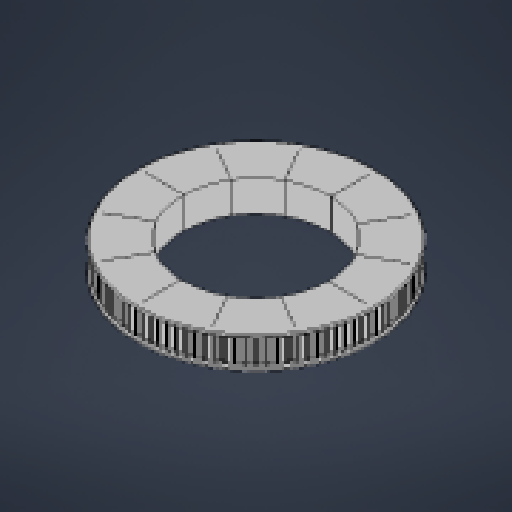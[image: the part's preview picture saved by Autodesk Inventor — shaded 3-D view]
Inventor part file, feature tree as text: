
AUTODESK INVENTOR PART (.ipt)
format: ipt  version: 2024 (Build 280153000, 153)  size: 1,488,896 bytes
history: native  units: mm
features: extrude x8, sketch x6, other x4, fillet x3, pattern_circular x2, revolve x1, mirror x1, hole x1, reference x1, projected_geometry x1
ambient origin geometry x8: Origin, YZ Plane, XZ Plane, XY Plane, X Axis, Y Axis, Z Axis, Center Point
bodies: Solid1 (feature_tree)
feature tree (28):
  extrude  "Extrusion1"  Depth=21.0mm
  extrude  "Extrusion2"  Depth=5.8mm
  extrude  "Extrusion3"  Depth=21.0mm
  fillet  "Fillet2"  [1 undecoded]
  pattern_circular  "Circular Pattern1"  [2 undecoded]
  revolve  "Revolution2"  [1 undecoded]
  mirror  "Mirror2"
  fillet  "Fillet5"  [1 undecoded]
  extrude  "Extrusion4"  TaperAngle=90.0deg  [1 undecoded]
  pattern_circular  "Circular Pattern2"  [2 undecoded]
  sketch  "Sketch7"  dims[d10=0.6mm]
  extrude  "Extrusion5"  Depth=2.5mm
  extrude  "Extrusion6"  Depth=19.5mm
  hole  "Hole1"  [1 undecoded]
  extrude  "Extrusion7"  Depth=2.5mm
  extrude  "Extrusion9"  Depth=2.5mm
  fillet  "Fillet1"  Radius=0.8mm
  sketch  "Sketch2"  dims[d0=29.0mm d2=21.0mm]
  sketch  "Sketch5"  dims[d3=0.0mm d5=5.8mm]
  sketch  "Sketch6"  dims[d7=1.565mm d8=21.0mm d9=0.0mm]
  reference  "Reference1"
  projected_geometry  "Projected Loop1"
  sketch  "Sketch8"  dims[d12=159.154943mm]
  sketch  "Sketch10"  dims[d13=0.0mm d14=0.0mm d15=0.6mm d16=1000.0mm d17=360.0deg d35=90.0deg d36=0.0mm d37=2.5mm d38=76.577472mm d39=5.1mm d40=2.5mm d41=2.5mm d42=0.8mm d43=0.05mm d44=75.577472mm d45=18.5mm d46=10.0mm d47=0.0mm d48=120.0mm d49=360.0deg d51=10.0mm d52=0.0mm d53=10.0mm d54=0.0mm d55=5.3mm d56=6.0mm d57=10.4mm d58=2.0mm d59=90.0deg d60=8.0mm d61=20.594885mm d62=7.0mm d63=40.0mm d65=360.0deg d67=19.5mm d68=0.0mm d73=65.0mm d74=65.0mm d75=3.490659mm d76=65.0mm d77=6.981317mm d78=12.5mm d79=135.0deg d80=40.0mm d82=360.0deg d84=0.0mm d85=0.0mm d71=0.0mm d72=0.0mm]
  other  "<userpath>\CodingProjects\C-AAM\CAD\V1\Base.iam"
  other  "Base.iam"
  other  "LazySusan:1"
  other  "IR:1"
note: 9 required parameter values undecoded (feature->parameter linkage not recoverable at this tier; creation-order binding heuristic only, values carry confidence <= 0.55)